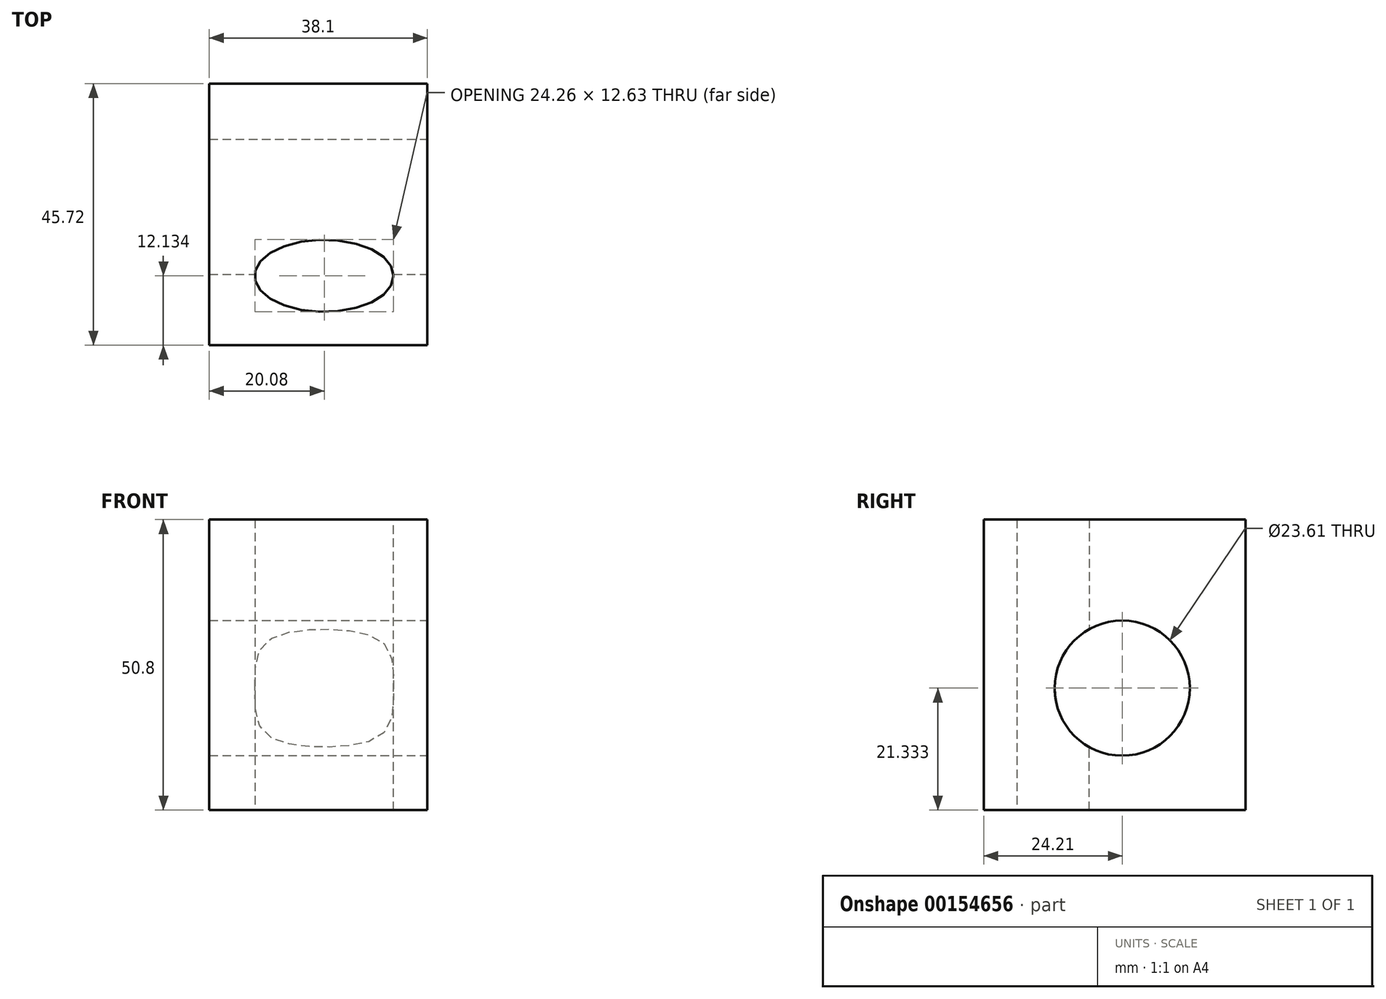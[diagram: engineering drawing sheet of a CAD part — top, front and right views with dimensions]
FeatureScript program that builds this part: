
annotation { "Feature Type Name" : "Feature", "Feature Type Description" : "" }
export const myFeature = defineFeature(function(context is Context, id is Id, definition is map)
    precondition{}
    {
        {
            var Q0;
            Q0=qCreatedBy(makeId("Front.planeOp"),FACE);
            var sketch = newSketch(context, id + "F0", { "sketchPlane" : qUnion([Q0])});
            skLineSegment(sketch, "E0.bottom", {"start": v(-20.08, 18.44) * mm, "end": v(18.02, 18.44) * mm});
            skLineSegment(sketch, "E0.top", {"start": v(-20.08, -32.36) * mm, "end": v(18.02, -32.36) * mm});
            skLineSegment(sketch, "E0.left", {"start": v(-20.08, 18.44) * mm, "end": v(-20.08, -32.36) * mm});
            skLineSegment(sketch, "E0.right", {"start": v(18.02, 18.44) * mm, "end": v(18.02, -32.36) * mm});
            skSolve(sketch);
        }
        {
            var Q0;
            Q0 = qSketchRegion(id + "F0", true);
            extrude(context, id + "F1", {"entities" : qUnion([Q0]), "depth" : 45.72 * mm});
        }
        {
            var Q0;
            Q0=makeQuery(id+"F1.opExtrude","SWEPT_FACE",FACE,{"disambiguationData":[OSD([sQuery(id+"F0.wireOp",EDGE,"E0.bottom")])]});
            var sketch = newSketch(context, id + "F2", { "sketchPlane" : qUnion([Q0])});
            skSolve(sketch);
        }
        {
            var Q0;
            {var subQ0=sQuery(id+"F0.wireOp",EDGE,"E0.bottom");Q0=makeQuery(id+"F2.imprint","IMPRINT",FACE,{"disambiguationData":[TD([[makeQuery(id+"F2.imprint","IMPRINT",EDGE,{"derivedFrom":makeQuery(id+"F1.opExtrude","CAP_EDGE",EDGE,{"disambiguationData":[OSD([subQ0])],"isStart":true})}),-1.0]])]});}
            var sketch = newSketch(context, id + "F3", { "sketchPlane" : qUnion([Q0])});
            skEllipse(sketch, "E1", {"center": v(0, -33.59) * mm, "majorRadius": 12.13 * mm, "minorRadius": 6.32 * mm, "majorAxis": v(1, 0)});
            skSolve(sketch);
        }
        {
            var Q0;
            Q0 = qSketchRegion(id + "F3", true);
            extrude(context, id + "F4", {"entities" : qUnion([Q0]), "operationType" : NewBodyOperationType.REMOVE, "oppositeDirection" : true, "depth" : 71.12 * mm});
        }
        {
            var Q0;
            Q0=makeQuery(id+"F1.opExtrude","SWEPT_FACE",FACE,{"disambiguationData":[OSD([sQuery(id+"F0.wireOp",EDGE,"E0.right")])]});
            var sketch = newSketch(context, id + "F5", { "sketchPlane" : qUnion([Q0])});
            skCircle(sketch, "E2", {"center": v(-21.51, -11.03) * mm, "radius": 11.8 * mm});
            skSolve(sketch);
        }
        {
            var Q0;
            Q0 = qSketchRegion(id + "F5", true);
            extrude(context, id + "F6", {"entities" : qUnion([Q0]), "operationType" : NewBodyOperationType.REMOVE, "oppositeDirection" : true, "depth" : 90.17 * mm});
        }
    });
